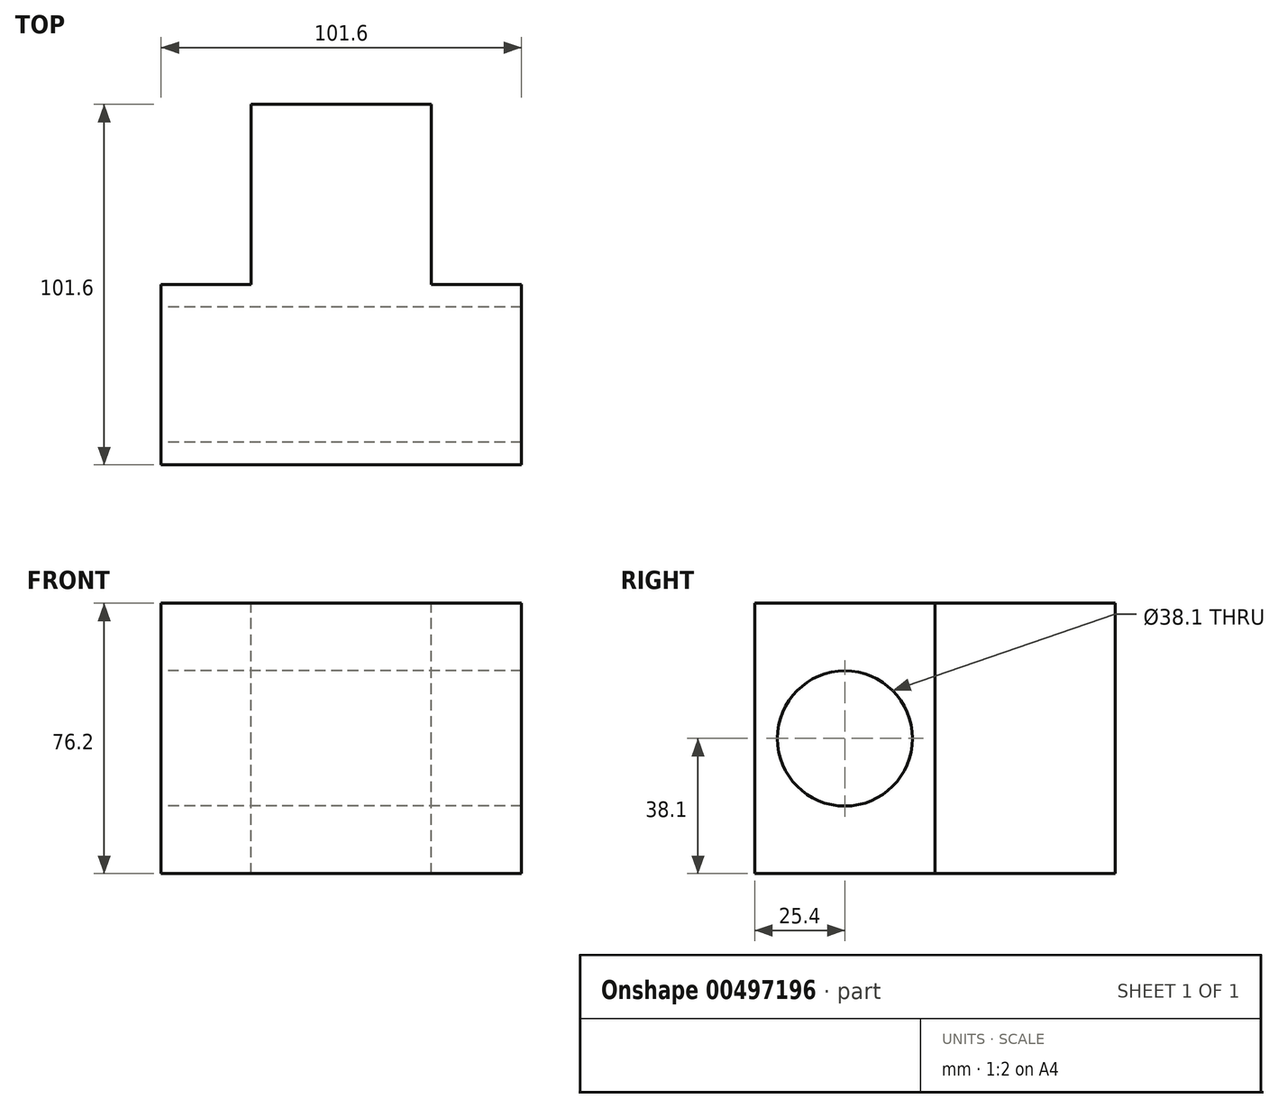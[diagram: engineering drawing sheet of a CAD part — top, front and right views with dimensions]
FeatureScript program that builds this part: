
annotation { "Feature Type Name" : "Feature", "Feature Type Description" : "" }
export const myFeature = defineFeature(function(context is Context, id is Id, definition is map)
    precondition{}
    {
        {
            var Q0;
            Q0=qCreatedBy(makeId("Top.planeOp"),FACE);
            var sketch = newSketch(context, id + "F0", { "sketchPlane" : qUnion([Q0])});
            skLineSegment(sketch, "E0.bottom", {"start": v(50.8, -25.4) * mm, "end": v(-50.8, -25.4) * mm});
            skLineSegment(sketch, "E0.top", {"start": v(50.8, 25.4) * mm, "end": v(-50.8, 25.4) * mm});
            skLineSegment(sketch, "E0.left", {"start": v(50.8, -25.4) * mm, "end": v(50.8, 25.4) * mm});
            skLineSegment(sketch, "E0.right", {"start": v(-50.8, -25.4) * mm, "end": v(-50.8, 25.4) * mm});
            skPoint(sketch, "E0.middle", {"position": v(0, 0) * mm});
            skPoint(sketch, "E1.endSnap0", {"position": v(0, 25.4) * mm});
            skLineSegment(sketch, "E2", {"start": v(0, 0) * mm, "end": v(0, 50.8) * mm});
            skLineSegment(sketch, "E3.bottom", {"start": v(25.4, 25.4) * mm, "end": v(-25.4, 25.4) * mm});
            skLineSegment(sketch, "E3.top", {"start": v(25.4, 76.2) * mm, "end": v(-25.4, 76.2) * mm});
            skLineSegment(sketch, "E3.left", {"start": v(25.4, 25.4) * mm, "end": v(25.4, 76.2) * mm});
            skLineSegment(sketch, "E3.right", {"start": v(-25.4, 25.4) * mm, "end": v(-25.4, 76.2) * mm});
            skPoint(sketch, "E3.middle", {"position": v(0, 50.8) * mm});
            skSolve(sketch);
        }
        {
            var Q0;
            Q0=makeQuery(id+"F0.imprint","IMPRINT",FACE,{"disambiguationData":[TD([[makeQuery(id+"F0.imprint","IMPRINT",EDGE,{"derivedFrom":sQuery(id+"F0.wireOp",EDGE,"E3.top")}),1.0]])]});
            var Q1;
            Q1=makeQuery(id+"F0.imprint","IMPRINT",FACE,{"disambiguationData":[TD([[makeQuery(id+"F0.imprint","IMPRINT",EDGE,{"derivedFrom":sQuery(id+"F0.wireOp",EDGE,"E0.bottom")}),-1.0]])]});
            extrude(context, id + "F1", {"entities" : qUnion([Q0, Q1]), "endBound" : BoundingType.SYMMETRIC, "oppositeDirection" : true, "depth" : 76.2 * mm});
        }
        {
            var Q0;
            Q0=makeQuery(id+"F1.opExtrude","SWEPT_FACE",FACE,{"disambiguationData":[OSD([sQuery(id+"F0.wireOp",EDGE,"E0.right")])]});
            var sketch = newSketch(context, id + "F2", { "sketchPlane" : qUnion([Q0])});
            skCircle(sketch, "E4", {"center": v(0, 0) * mm, "radius": 19.05 * mm});
            skSolve(sketch);
        }
        {
            var Q0;
            Q0=makeQuery(id+"F2.imprint","IMPRINT",FACE,{"disambiguationData":[TD([[makeQuery(id+"F2.imprint","IMPRINT",EDGE,{"derivedFrom":sQuery(id+"F2.wireOp",EDGE,"E4")}),1.0]])]});
            extrude(context, id + "F3", {"entities" : qUnion([Q0]), "operationType" : NewBodyOperationType.REMOVE, "endBound" : BoundingType.UP_TO_NEXT, "oppositeDirection" : true, "depth" : 63.5 * mm, "offsetDistance" : 25.4 * mm});
        }
    });
